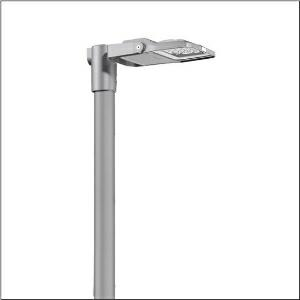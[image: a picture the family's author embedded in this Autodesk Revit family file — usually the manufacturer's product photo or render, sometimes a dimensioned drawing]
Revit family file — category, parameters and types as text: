
# Revit family: floodlight_fl_21_iq_micro___pl52_5xa7762a4d3a_1d61
name_source: partatom
category: Lighting Fixtures
units: mm (PartAtom-declared; Revit-internal decimal feet)

## family parameters
Cut with Voids When Loaded = No
Host = Face
Light Source = No
Part Type = Normal
Room Calculation Point = No
Round Connector Dimension = Use Diameter
Shared = No

## types (1)
- --- (1 x LED, 3010 lm, 23.1 W, 4000K)
    Apparent Load = 23 VA
    CIE Flux Codes = 26 60 98 100 100
    Color Rendering = 70
    Color Temperature = 4000K
    Default Elevation = 1800 mm
    Description = Floodlight FL 21 iQ micro, floodlight, primary light control with lens, of PMMA, primary optical cover: protective disc, of toughened safety glass, transparent, light distribution: PL52, light emission: direct distribution, installation type: surface-mounted, LED, High Power LED, rated luminous flux: 3.010lm, luminous efficacy: 130lm/W, light colour: 740, colour temperature: 4000K, control gear: iQ Street-Remote/DALI, control: Auto-Match, Temp-Guard, Night-Set, Smart-Wire, Desk-Remote (wireless, voltage-free reading and setting of iQ features in the workshop via application-optimized NFC function/RFID function), optimised constant luminous flux control (CLO 2.0), Street-Remote, with terminal, 6-pole, mains connection: 220..240V, AC, 50/60Hz, start of lifetime: 23W, end of service life: 24W, reduction: 11W, luminaire housing, of diecast aluminium, powder-coated, Siteco® metallic grey (DB 702S), corrosivity category C5 mid according to DIN EN ISO 12944, suitable for swimming pools, chlorine-resistant, sealing non-destructively replaceable, please order mast flange separately, mast bracket, of steel, galvanised, powder-coated, Siteco® metallic grey (DB 702S), protection rating (complete): IP66, insulation class (complete): insulation class II (safety insulation), certification: CE, ENEC, VDE, protection symbol: D, impact resistance: IK07, permissible operating ambient temperature: -40..+40°C, permissible operating ambient temperature for outdoor applications: -40..+50°C, standard: DIN EN 12944, LABS conformity tested according to VDMA 24364:2018-05, packaging unit: 1 piece

Light Distribution: PL52
    Height = 65 mm
    Lamp = 1 x LED
    Lamp Light Flux = 3010 lm
    Lamp Power = 23.1 W
    Lamp count = 1
    Length = 312 mm
    Luminous efficacy = 130 lm/W
    Manufacturer = Siteco
    ModVariant = No
    Model = 5XA7762A4D3A
    Number of Poles = 1
    OnlyDefault = Yes
    Power Factor = 1
    Product Name = Floodlight FL 21 iQ micro | PL52
    Product group = floodlight | pylon annexe
    ProductGroupID = 6201
    Protection Class = Protection class II
    Protection Degree = IP 66
    RLX_Detail_Level = 1
    RLX_Emergency_Light_Flux = 0 lm
    RLX_Emergency_Type = 0
    RLX_Emergency_Type_DB = No
    RlxData = <blob elided: 102069 chars, md5=4a8890b8>
    Socket = socket
    Standby Power = 0 W
    System Light Flux = 3010 lm
    System Power = 23 W
    Type Comments = factory setting: luminous flux: 100 % | dim-lin: 254 | 455 mA
    Type Image = l_1007121.jpg
    URL = http://relux.com
    VarID = @adj_199207
    Voltage = 0 V
    Weight = 0.00 kg
    Width = 230 mm

## geometry (parser evidence)
native form markers: Blend x4, Sweep x11
no freeform markers — native parametric forms only
